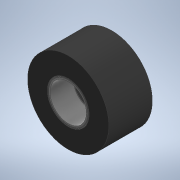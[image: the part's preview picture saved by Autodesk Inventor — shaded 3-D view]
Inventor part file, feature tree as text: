
AUTODESK INVENTOR PART (.ipt)
format: ipt  version: 2022 (Build 260153000, 153)  size: 356,352 bytes
history: native  units: in
note: dims shown in document units (in); Inventor stores cm internally (conversion verified against a paired STEP export)
features: sketch x3, fillet x2, extrude x2, revolve x1
ambient origin geometry x8: Origin, YZ Plane, XZ Plane, XY Plane, X Axis, Y Axis, Z Axis, Center Point
bodies: Solid1 (feature_tree)
feature tree (8):
  revolve  "Revolution1"  [1 undecoded]
  fillet  "Fillet1"  Radius=0.6875in
  extrude  "Extrusion1"  Depth=0.3125in
  extrude  "Extrusion2"  Depth=0.275in
  fillet  "Fillet3"  Radius=0.1875in
  sketch  "Sketch1"  dims[d0=1.4in d1=1.5in d2=0.6875in]
  sketch  "Sketch2"  dims[d3=0.0625in d4=0.3125in d5=0.5625in]
  sketch  "Sketch3"  dims[d6=0.125in d7=0.275in d9=0.1875in d11=0.125in d12=360.0deg d13=0.0197in d14=0.0039in d15=0.0197in d16=0.0039in d17=0.0312in d19=0.625in d20=0.325in d21=0.64in d22=0.15in d23=0.25in d24=0.7874in d26=360.0deg d28=1.0in d29=0.0in d30=0.625in d31=0.138in d32=0.7874in d34=360.0deg d36=0.0in d37=0.0in d38=0.0197in d39=0.125in]
note: 1 required parameter value undecoded (feature->parameter linkage not recoverable at this tier; creation-order binding heuristic only, values carry confidence <= 0.55)
